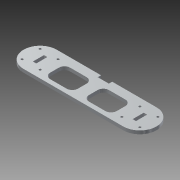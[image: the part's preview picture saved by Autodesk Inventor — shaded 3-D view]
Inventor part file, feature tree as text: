
AUTODESK INVENTOR PART (.ipt)
format: ipt  version: 2013 (Build 170138000, 138)  size: 168,960 bytes
history: native  units: mm
features: extrude x1, sketch x1
ambient origin geometry x8: Origin, YZ Plane, XZ Plane, XY Plane, X Axis, Y Axis, Z Axis, Center Point
feature tree (2):
  extrude  "Extrusion4"  Depth=120.0mm
  sketch  "Sketch1"  dims[d0=30.0mm d1=120.0mm d2=10.0mm d3=3.0mm d4=13.5mm d5=10.0mm d6=87.0mm d7=3.0mm d8=10.0mm d9=10.0mm d10=15.0mm d11=10.0mm d12=55.0mm d13=3.0mm d16=5.0mm d17=5.0mm d18=30.0mm d19=30.0mm d20=5.0mm d23=25.0mm d24=25.0mm d25=5.0mm d27=8.0mm d30=2.0mm d31=8.132mm d32=8.132mm d33=40.0mm d35=360.0deg d37=2.0mm d40=8.132mm d41=8.132mm d42=40.0mm d44=360.0deg d46=3.0mm d47=0.0mm d48=18.0mm d50=3.0mm d51=15.0mm]
